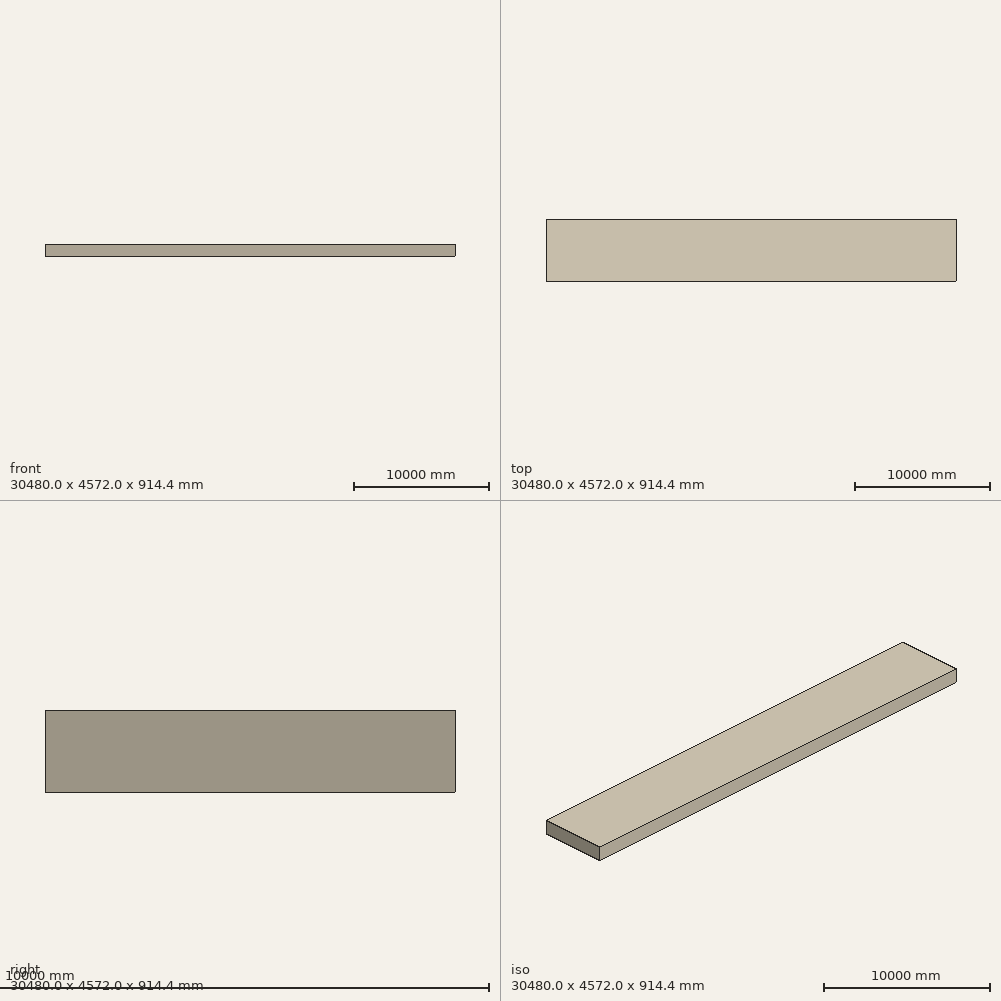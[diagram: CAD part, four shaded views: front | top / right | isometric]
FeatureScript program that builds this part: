
annotation { "Feature Type Name" : "Feature", "Feature Type Description" : "" }
export const myFeature = defineFeature(function(context is Context, id is Id, definition is map)
    precondition{}
    {
        {
            var Q0;
            Q0=qCreatedBy(makeId("Top.planeOp"),FACE);
            var sketch = newSketch(context, id + "F0", { "sketchPlane" : qUnion([Q0])});
            skLineSegment(sketch, "E0", {"start": v(0, 0) * mm, "end": v(0, 4572) * mm});
            skLineSegment(sketch, "E1", {"start": v(0, 4572) * mm, "end": v(30480, 4572) * mm});
            skLineSegment(sketch, "E2", {"start": v(30480, 4572) * mm, "end": v(30480, 0) * mm});
            skLineSegment(sketch, "E3", {"start": v(30480, 0) * mm, "end": v(0, 0) * mm});
            skSolve(sketch);
        }
        {
            var Q0;
            Q0=makeQuery(id+"F0.imprint","IMPRINT",FACE,{"disambiguationData":[TD([[makeQuery(id+"F0.imprint","IMPRINT",EDGE,{"derivedFrom":sQuery(id+"F0.wireOp",EDGE,"E0")}),-1.0]])]});
            extrude(context, id + "F1", {"entities" : qUnion([Q0]), "oppositeDirection" : true, "depth" : 914.4 * mm, "offsetDistance" : 25.4 * mm});
        }
    });
